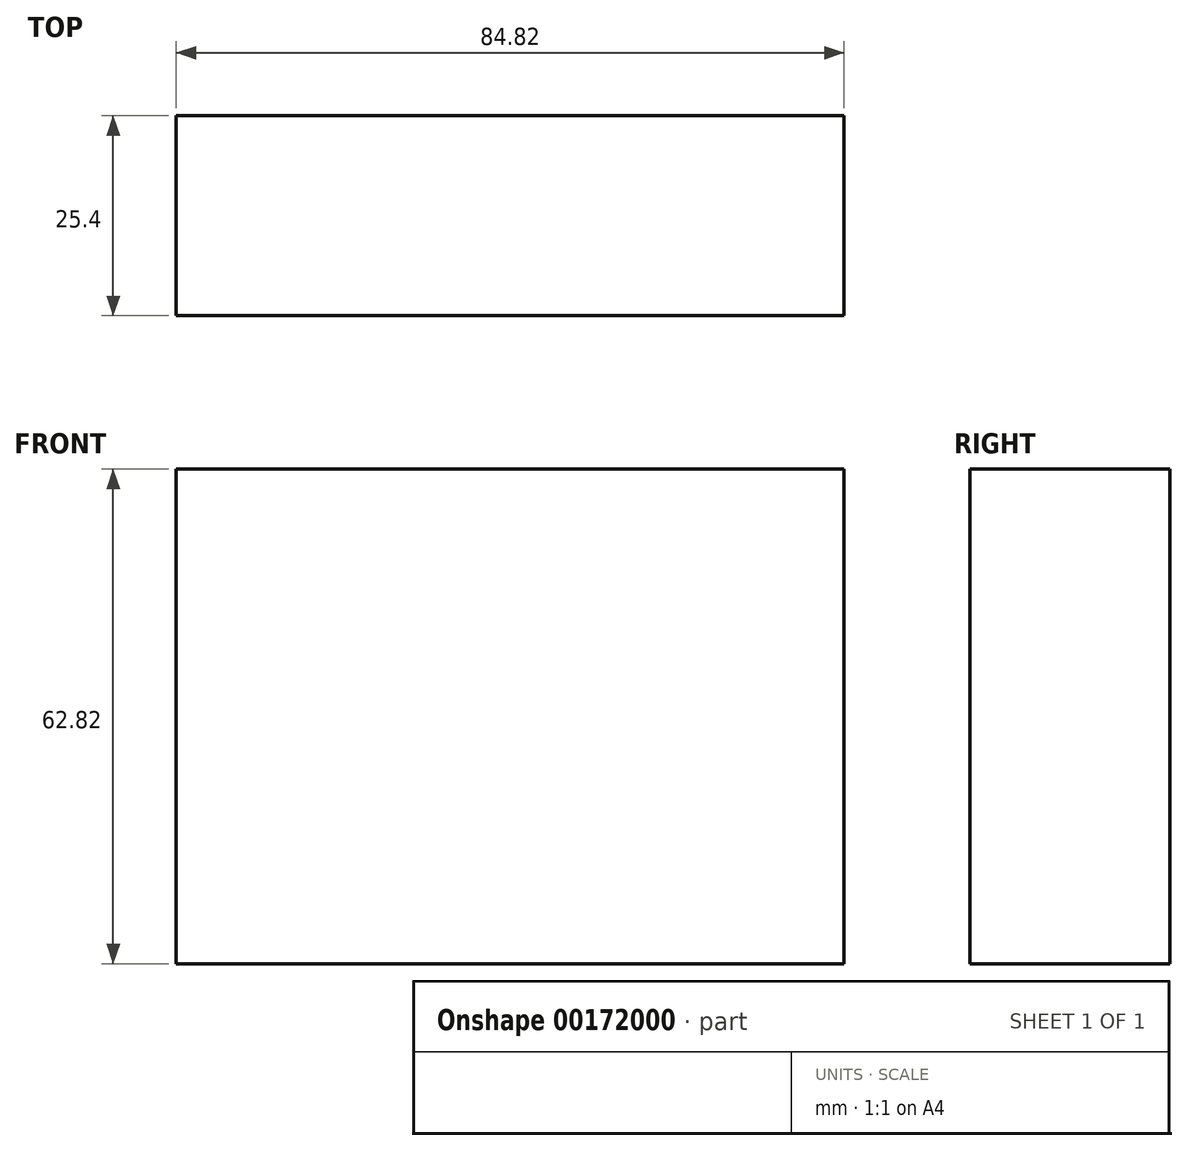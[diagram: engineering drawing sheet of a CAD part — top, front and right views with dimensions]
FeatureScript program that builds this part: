
annotation { "Feature Type Name" : "Feature", "Feature Type Description" : "" }
export const myFeature = defineFeature(function(context is Context, id is Id, definition is map)
    precondition{}
    {
        {
            var Q0;
            Q0=qCreatedBy(makeId("Front.planeOp"),FACE);
            var sketch = newSketch(context, id + "F0", { "sketchPlane" : qUnion([Q0])});
            skLineSegment(sketch, "E0.bottom", {"start": v(-48.21, 53.22) * mm, "end": v(36.6, 53.22) * mm});
            skLineSegment(sketch, "E0.top", {"start": v(-48.21, -9.6) * mm, "end": v(36.6, -9.6) * mm});
            skLineSegment(sketch, "E0.left", {"start": v(-48.21, 53.22) * mm, "end": v(-48.21, -9.6) * mm});
            skLineSegment(sketch, "E0.right", {"start": v(36.6, 53.22) * mm, "end": v(36.6, -9.6) * mm});
            skSolve(sketch);
        }
        {
            var Q0;
            Q0=makeQuery(id+"F0.imprint","IMPRINT",FACE,{"disambiguationData":[TD([[makeQuery(id+"F0.imprint","IMPRINT",EDGE,{"derivedFrom":sQuery(id+"F0.wireOp",EDGE,"E0.bottom")}),-1.0]])]});
            extrude(context, id + "F1", {"entities" : qUnion([Q0]), "depth" : 25.4 * mm});
        }
    });
